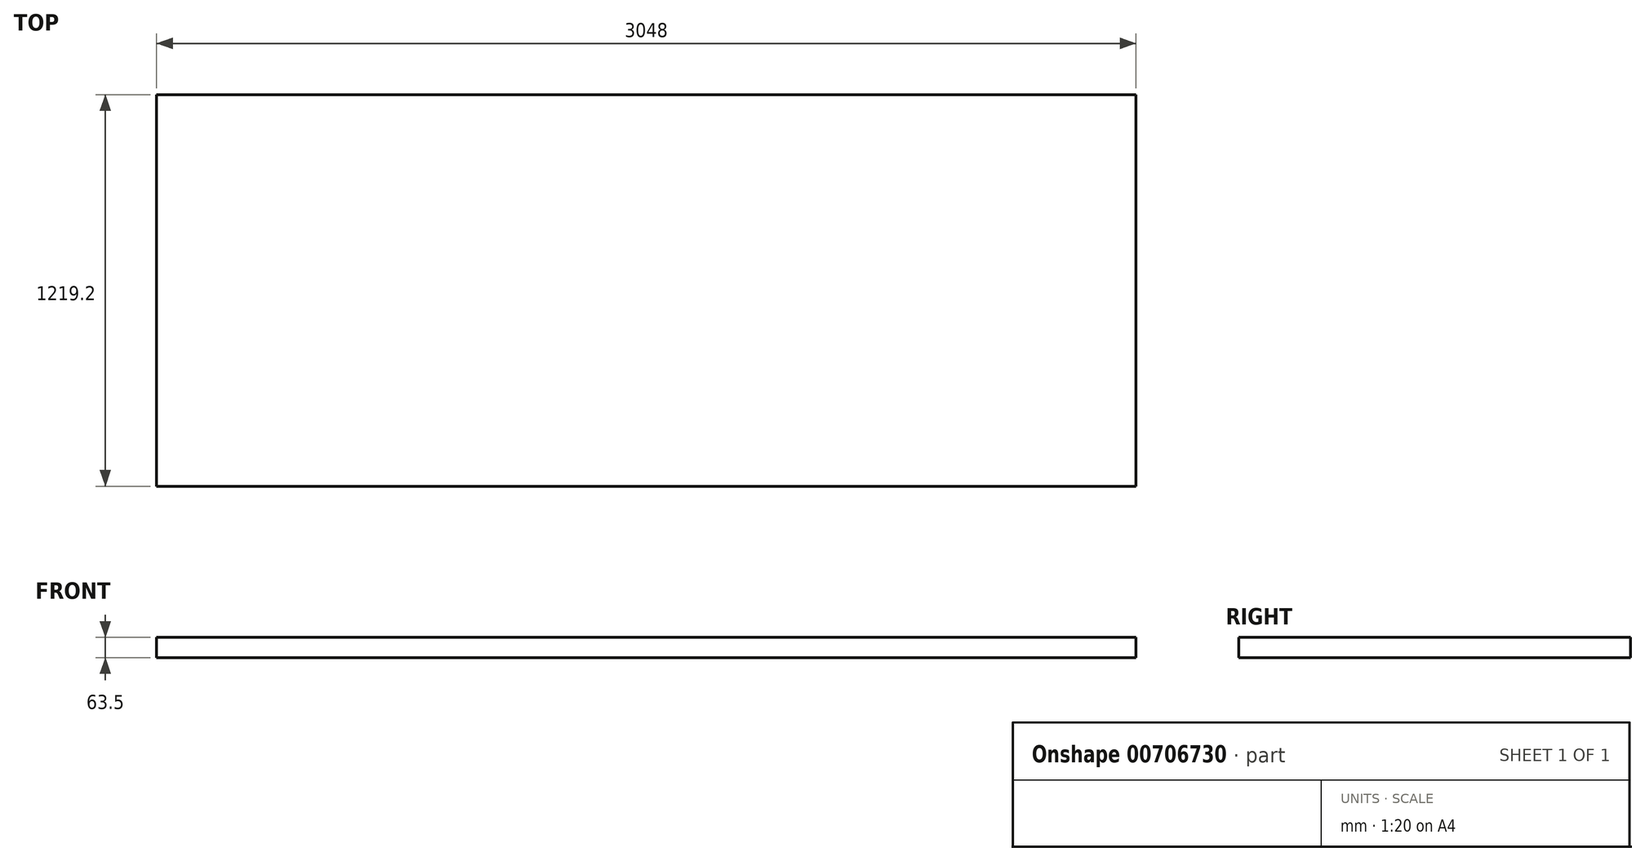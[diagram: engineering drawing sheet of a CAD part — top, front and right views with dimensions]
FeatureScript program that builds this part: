
annotation { "Feature Type Name" : "Feature", "Feature Type Description" : "" }
export const myFeature = defineFeature(function(context is Context, id is Id, definition is map)
    precondition{}
    {
        {
            var Q0;
            Q0=qCreatedBy(makeId("Top.planeOp"),FACE);
            var sketch = newSketch(context, id + "F0", { "sketchPlane" : qUnion([Q0])});
            skLineSegment(sketch, "E0.bottom", {"start": v(1524, 609.6) * mm, "end": v(-1524, 609.6) * mm});
            skLineSegment(sketch, "E0.top", {"start": v(1524, -609.6) * mm, "end": v(-1524, -609.6) * mm});
            skLineSegment(sketch, "E0.left", {"start": v(1524, 609.6) * mm, "end": v(1524, -609.6) * mm});
            skLineSegment(sketch, "E0.right", {"start": v(-1524, 609.6) * mm, "end": v(-1524, -609.6) * mm});
            skPoint(sketch, "E0.middle", {"position": v(0, 0) * mm});
            skSolve(sketch);
        }
        {
            var Q0;
            Q0=makeQuery(id+"F0.imprint","IMPRINT",FACE,{"disambiguationData":[TD([[makeQuery(id+"F0.imprint","IMPRINT",EDGE,{"derivedFrom":sQuery(id+"F0.wireOp",EDGE,"E0.bottom")}),1.0]])]});
            extrude(context, id + "F1", {"entities" : qUnion([Q0]), "depth" : 63.5 * mm, "offsetDistance" : 25.4 * mm});
        }
    });
